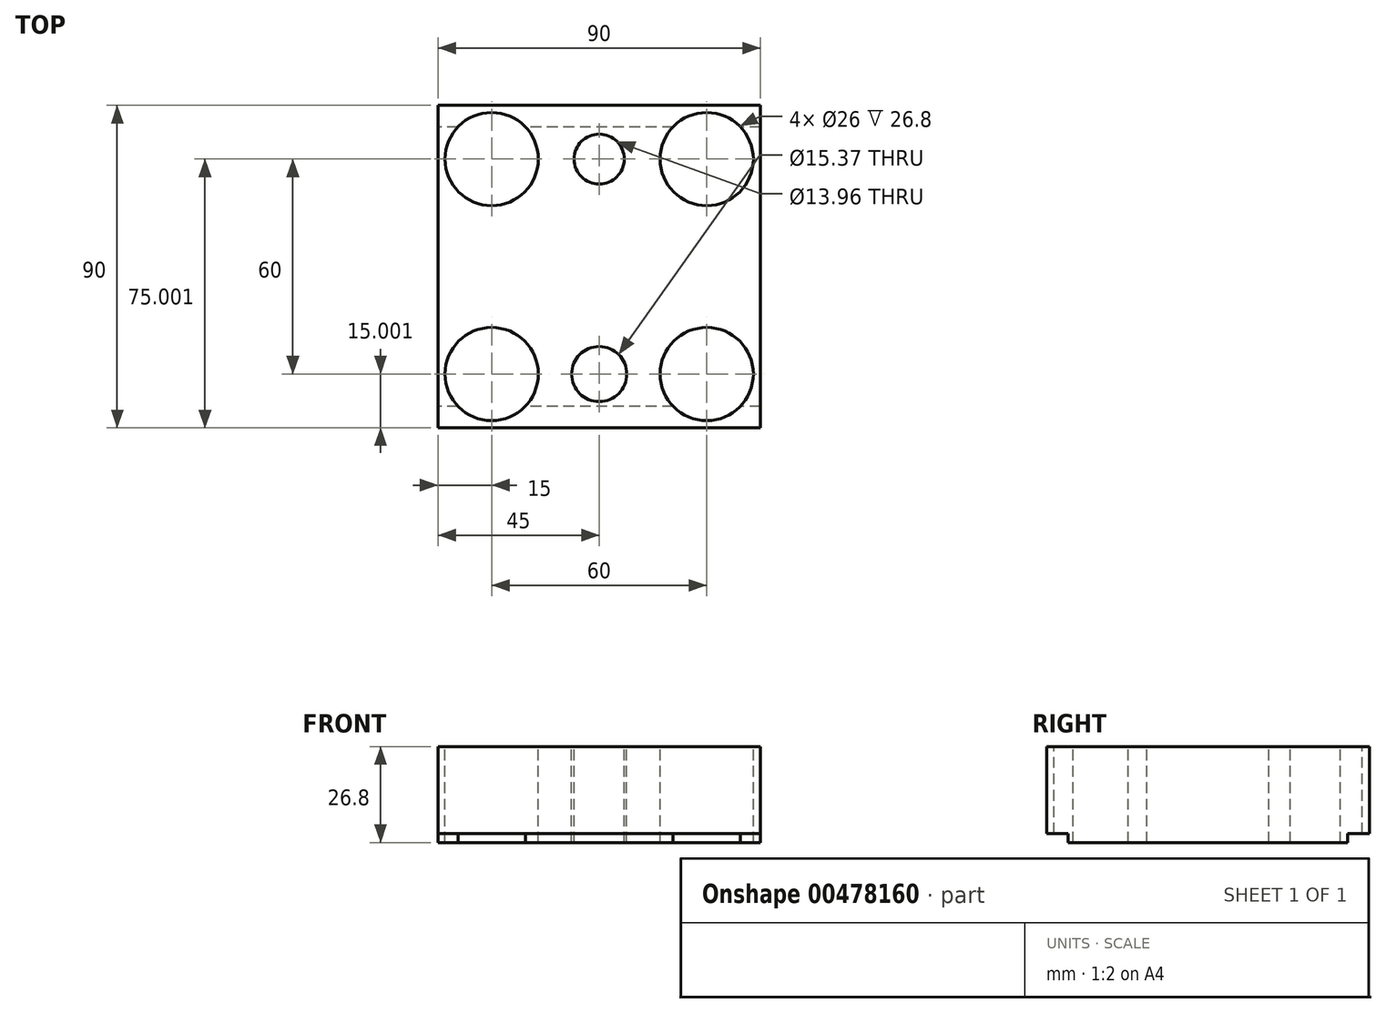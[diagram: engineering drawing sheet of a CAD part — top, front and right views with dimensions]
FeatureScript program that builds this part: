
annotation { "Feature Type Name" : "Feature", "Feature Type Description" : "" }
export const myFeature = defineFeature(function(context is Context, id is Id, definition is map)
    precondition{}
    {
        {
            var Q0;
            Q0=qCreatedBy(makeId("Right.planeOp"),FACE);
            var sketch = newSketch(context, id + "F0", { "sketchPlane" : qUnion([Q0])});
            skLineSegment(sketch, "E0", {"start": v(-43.44, -9.63) * mm, "end": v(34.56, -9.63) * mm});
            skLineSegment(sketch, "E1", {"start": v(34.56, -9.63) * mm, "end": v(34.56, -7.13) * mm});
            skLineSegment(sketch, "E2", {"start": v(34.56, -7.13) * mm, "end": v(40.56, -7.13) * mm});
            skLineSegment(sketch, "E3", {"start": v(40.56, -7.13) * mm, "end": v(40.56, 17.17) * mm});
            skLineSegment(sketch, "E4", {"start": v(40.56, 17.17) * mm, "end": v(-49.44, 17.17) * mm});
            skLineSegment(sketch, "E5", {"start": v(-49.44, 17.17) * mm, "end": v(-49.44, -7.13) * mm});
            skLineSegment(sketch, "E6", {"start": v(-49.44, -7.13) * mm, "end": v(-43.44, -7.13) * mm});
            skLineSegment(sketch, "E7", {"start": v(-43.44, -7.13) * mm, "end": v(-43.44, -9.63) * mm});
            skSolve(sketch);
        }
        {
            var Q0;
            Q0=makeQuery(id+"F0.imprint","IMPRINT",FACE,{"disambiguationData":[TD([[makeQuery(id+"F0.imprint","IMPRINT",EDGE,{"derivedFrom":sQuery(id+"F0.wireOp",EDGE,"E0")}),1.0]])]});
            extrude(context, id + "F1", {"entities" : qUnion([Q0]), "depth" : 90 * mm});
        }
        {
            var Q0;
            Q0=makeQuery(id+"F1.opExtrude","SWEPT_FACE",FACE,{"disambiguationData":[OSD([sQuery(id+"F0.wireOp",EDGE,"E4")])]});
            var sketch = newSketch(context, id + "F2", { "sketchPlane" : qUnion([Q0])});
            skCircle(sketch, "E8", {"center": v(75, 25.56) * mm, "radius": 13 * mm});
            skCircle(sketch, "E9", {"center": v(15, -34.44) * mm, "radius": 13 * mm});
            skCircle(sketch, "E10", {"center": v(75, -34.44) * mm, "radius": 13 * mm});
            skCircle(sketch, "E11", {"center": v(45, -34.44) * mm, "radius": 7.69 * mm});
            skCircle(sketch, "E12", {"center": v(45, 25.56) * mm, "radius": 6.98 * mm});
            skCircle(sketch, "E13", {"center": v(15, 25.56) * mm, "radius": 13 * mm});
            skSolve(sketch);
        }
        {
            var Q0;
            Q0 = qSketchRegion(id + "F2", true);
            extrude(context, id + "F3", {"entities" : qUnion([Q0]), "operationType" : NewBodyOperationType.REMOVE, "endBound" : BoundingType.UP_TO_NEXT, "oppositeDirection" : true, "depth" : 25 * mm});
        }
    });
